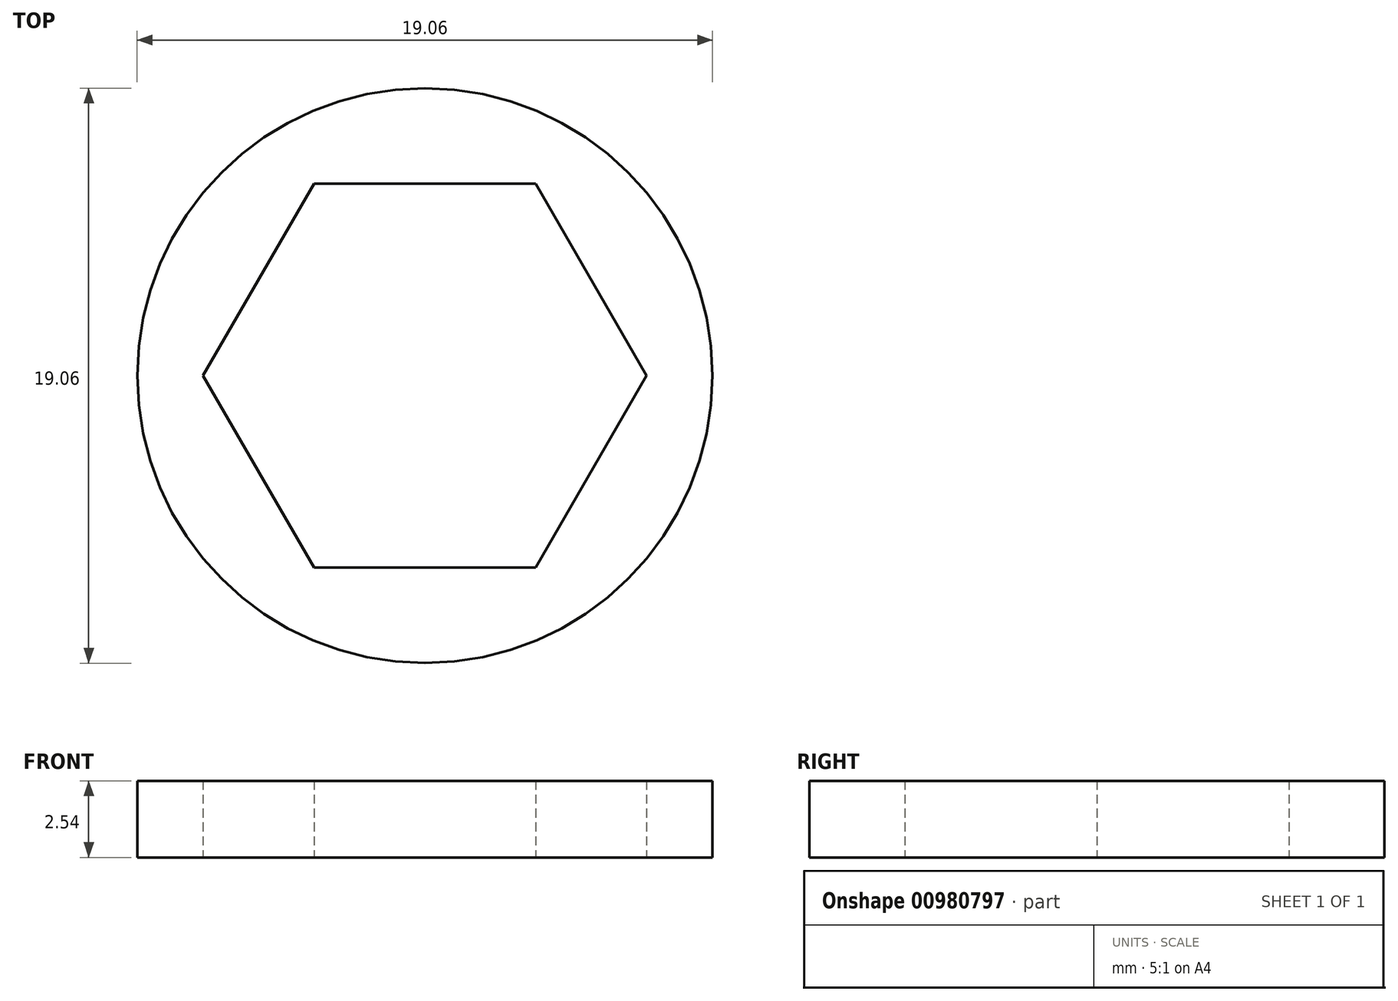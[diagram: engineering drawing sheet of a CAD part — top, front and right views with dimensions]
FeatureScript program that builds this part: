
annotation { "Feature Type Name" : "Feature", "Feature Type Description" : "" }
export const myFeature = defineFeature(function(context is Context, id is Id, definition is map)
    precondition{}
    {
        {
            var Q0;
            Q0=qCreatedBy(makeId("Top.planeOp"),FACE);
            var sketch = newSketch(context, id + "F0", { "sketchPlane" : qUnion([Q0])});
            skCircle(sketch, "E0", {"center": v(0, 0) * mm, "radius": 9.53 * mm});
            skCircle(sketch, "E1.cCircle", {"center": v(0, 0) * mm, "radius": 6.36 * mm, "construction": true});
            skLineSegment(sketch, "E1.0", {"start": v(-3.67, 6.36) * mm, "end": v(3.67, 6.36) * mm});
            skLineSegment(sketch, "E1.1", {"start": v(3.67, 6.36) * mm, "end": v(7.35, 0) * mm});
            skLineSegment(sketch, "E1.2", {"start": v(7.35, 0) * mm, "end": v(3.67, -6.36) * mm});
            skLineSegment(sketch, "E1.3", {"start": v(3.67, -6.36) * mm, "end": v(-3.67, -6.36) * mm});
            skLineSegment(sketch, "E1.4", {"start": v(-3.67, -6.36) * mm, "end": v(-7.35, 0) * mm});
            skLineSegment(sketch, "E1.5", {"start": v(-7.35, 0) * mm, "end": v(-3.67, 6.36) * mm});
            skPoint(sketch, "E1.0.midPoint", {"position": v(0, 6.36) * mm});
            skSolve(sketch);
        }
        {
            var Q0;
            Q0=qSketchRegion(id+"F0",true);
            extrude(context, id + "F1", {"entities" : qUnion([Q0]), "depth" : 2.54 * mm, "offsetDistance" : 25.4 * mm});
        }
    });
